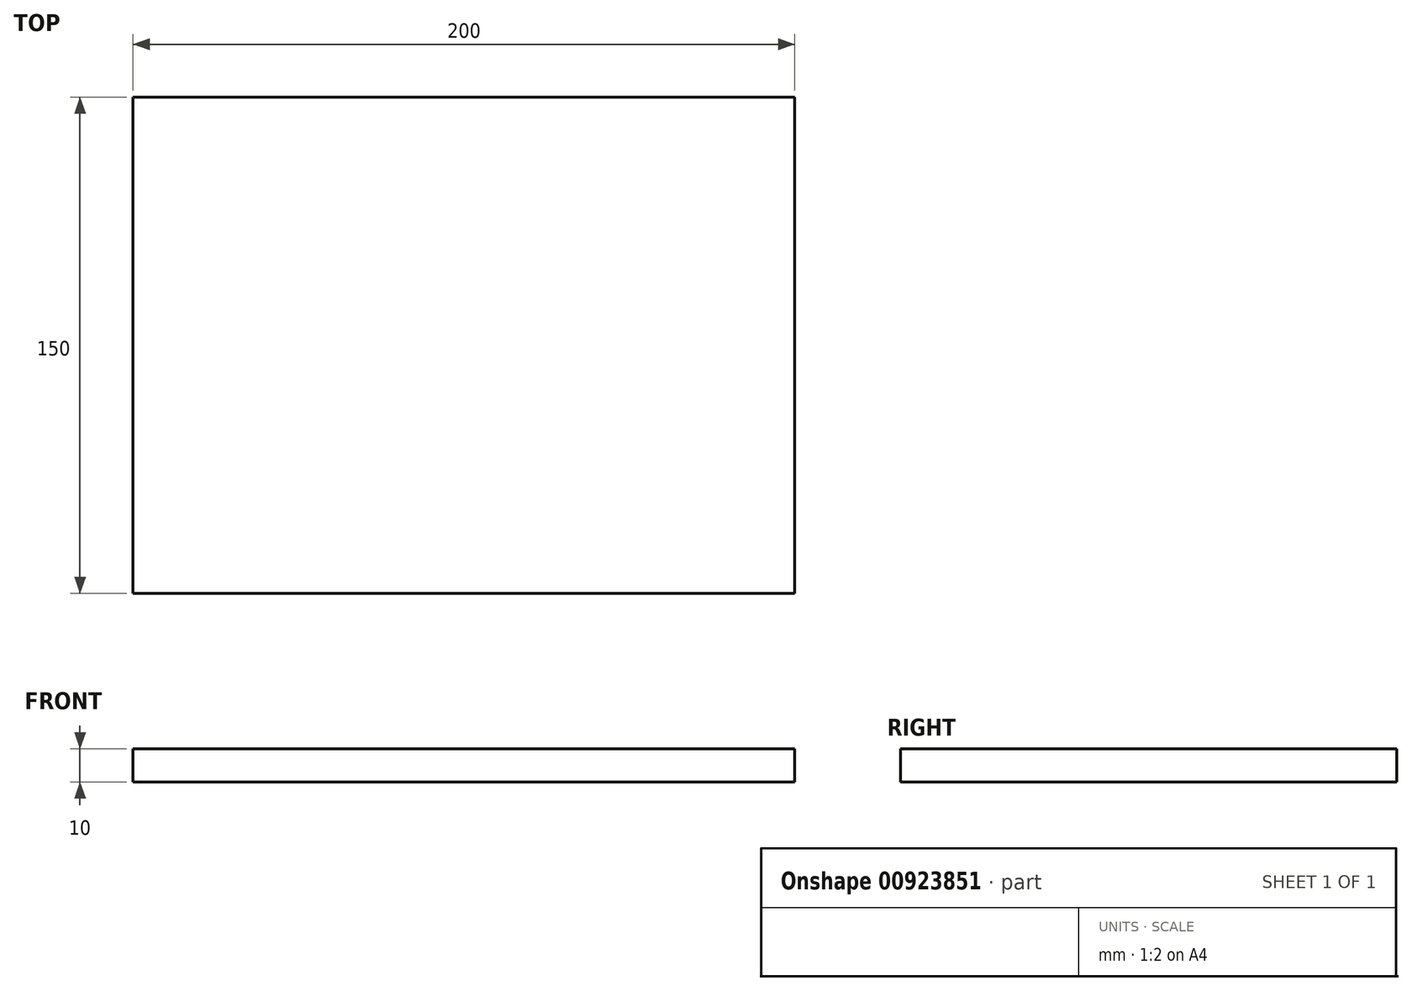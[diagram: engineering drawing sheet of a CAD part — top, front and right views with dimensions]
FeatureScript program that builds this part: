
annotation { "Feature Type Name" : "Feature", "Feature Type Description" : "" }
export const myFeature = defineFeature(function(context is Context, id is Id, definition is map)
    precondition{}
    {
        {
            var Q0;
            Q0=qCreatedBy(makeId("Top.planeOp"),FACE);
            var sketch = newSketch(context, id + "F0", { "sketchPlane" : qUnion([Q0])});
            skLineSegment(sketch, "E0.bottom", {"start": v(100, 75) * mm, "end": v(-100, 75) * mm});
            skLineSegment(sketch, "E0.top", {"start": v(100, -75) * mm, "end": v(-100, -75) * mm});
            skLineSegment(sketch, "E0.left", {"start": v(100, 75) * mm, "end": v(100, -75) * mm});
            skLineSegment(sketch, "E0.right", {"start": v(-100, 75) * mm, "end": v(-100, -75) * mm});
            skPoint(sketch, "E0.middle", {"position": v(0, 0) * mm});
            skSolve(sketch);
        }
        {
            var Q0;
            Q0=makeQuery(id+"F0.imprint","IMPRINT",FACE,{"disambiguationData":[TD([[makeQuery(id+"F0.imprint","IMPRINT",EDGE,{"derivedFrom":sQuery(id+"F0.wireOp",EDGE,"E0.bottom")}),1.0]])]});
            var Q1;
            Q1=makeQuery(id+"F0.imprint","IMPRINT",FACE,{"disambiguationData":[TD([[makeQuery(id+"F0.imprint","IMPRINT",EDGE,{"derivedFrom":sQuery(id+"F0.wireOp",EDGE,"DOfoMCcq-8ObT-myeJ-42Uw-S4tERSy3AE3O.bottom")}),1.0]])]});
            extrude(context, id + "F1", {"entities" : qUnion([Q0, Q1]), "depth" : 10 * mm, "offsetDistance" : 25 * mm});
        }
    });
